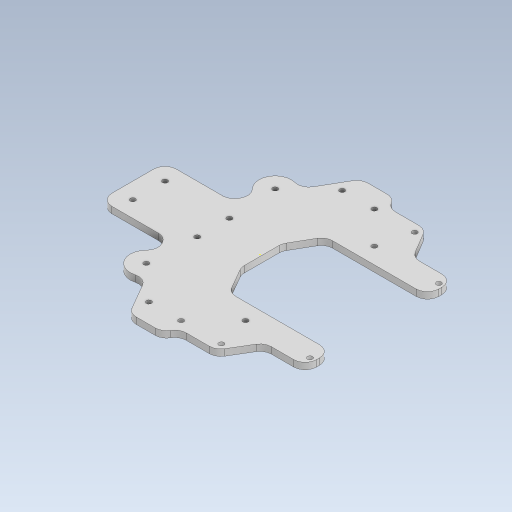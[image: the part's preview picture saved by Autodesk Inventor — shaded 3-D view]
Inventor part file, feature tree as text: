
AUTODESK INVENTOR PART (.ipt)
format: ipt  version: 2023.5 (Build 275446000, 446)  size: 438,784 bytes
history: native  units: mm
features: sketch x2, extrude x2, fillet x1
ambient origin geometry x8: Origin, YZ Plane, XZ Plane, XY Plane, X Axis, Y Axis, Z Axis, Center Point
bodies: Solid1 (feature_tree)
feature tree (5):
  sketch  "Sketch1"  dims[d0=3.2mm d3=3.2mm]
  extrude  "Extrusion1"  Depth=3.2mm
  sketch  "Sketch2"  dims[d5=3.2mm d6=50.0mm d15=20.0mm d16=40.0mm d17=120.0deg d18=20.0mm d23=4.0mm d24=0.0mm d25=3.2mm d27=40.0mm d28=120.0deg d29=3.2mm d30=40.0mm d31=55.0mm d32=15.981mm d33=120.0deg d34=4.0mm d35=0.0mm d36=3.2mm d37=30.0mm d38=20.0mm d39=3.2mm d40=25.0mm d41=7.0mm]
  extrude  "Extrusion2"  Depth=50.0mm
  fillet  "Fillet1"  Radius=20.0mm
